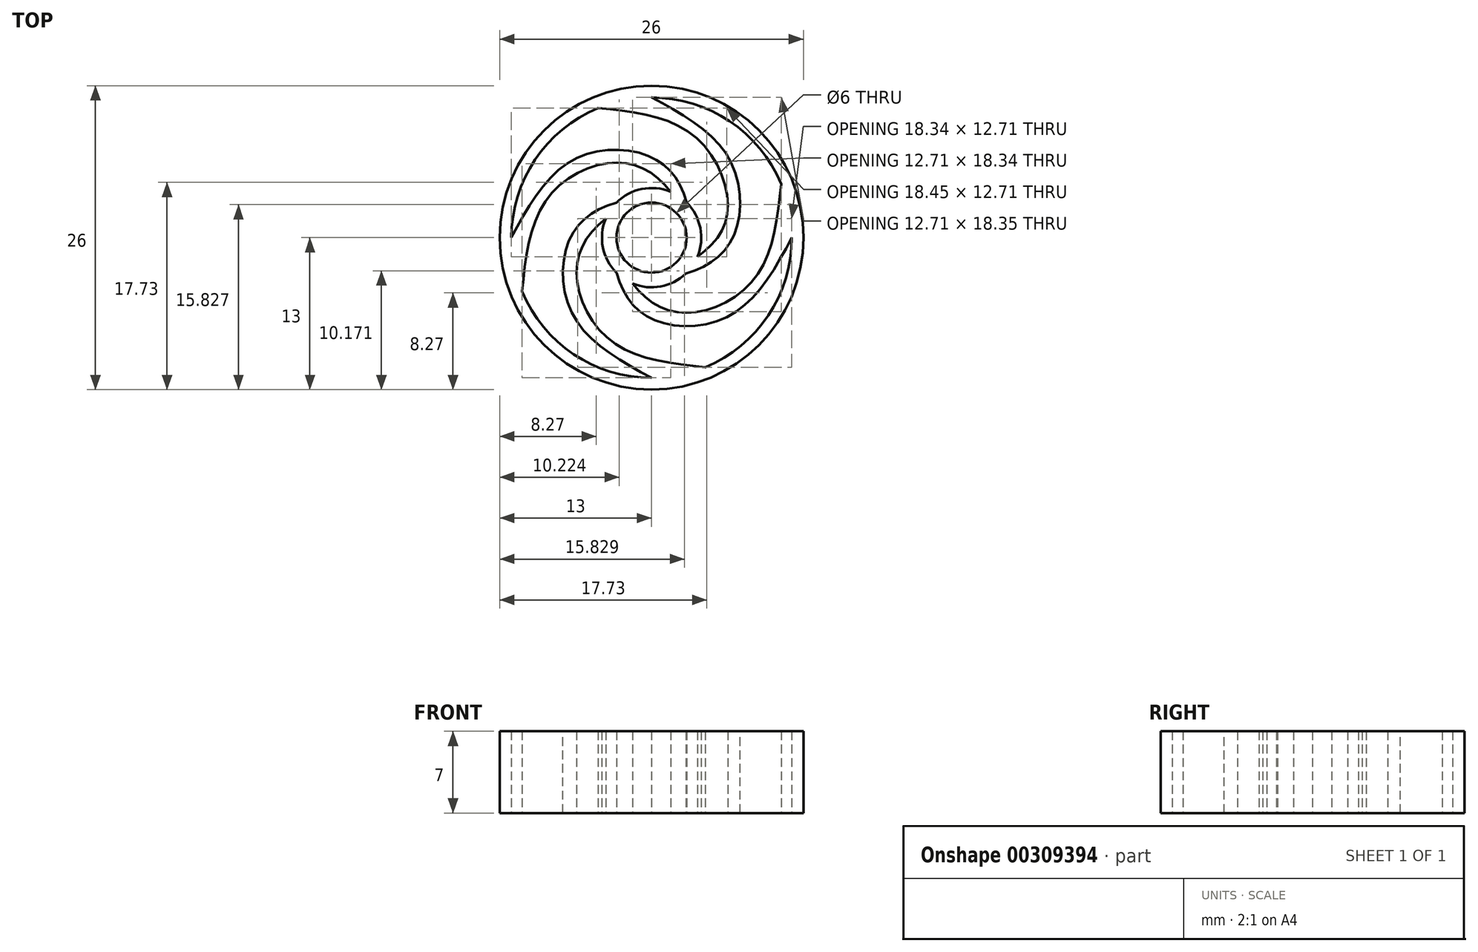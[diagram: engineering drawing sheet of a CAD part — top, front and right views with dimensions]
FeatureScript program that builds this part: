
annotation { "Feature Type Name" : "Feature", "Feature Type Description" : "" }
export const myFeature = defineFeature(function(context is Context, id is Id, definition is map)
    precondition{}
    {
        {
            var Q0;
            Q0=qCreatedBy(makeId("Top.planeOp"),FACE);
            var sketch = newSketch(context, id + "F0", { "sketchPlane" : qUnion([Q0])});
            skCircle(sketch, "E0", {"center": v(0, 0) * mm, "radius": 3 * mm});
            skCircle(sketch, "E1", {"center": v(0, 0) * mm, "radius": 4.25 * mm});
            skCircle(sketch, "E2", {"center": v(0, 0) * mm, "radius": 12 * mm});
            skFitSpline(sketch, "E3", {"points": [v(-11.09, 4.6) * mm, v(-3.61, 8.73) * mm, v(2.66, 6.42) * mm, v(3.93, 1.63) * mm], "startDerivative": vector(18.7, 15.37) * mm, "endDerivative": vector(-2.28, -19.06) * mm});
            skFitSpline(sketch, "E4", {"points": [v(-8.49, 8.49) * mm, v(0, 9.44) * mm, v(4.85, 4.98) * mm, v(4.25, 0) * mm], "startDerivative": vector(23.2, 7) * mm, "endDerivative": vector(-9.1, -16.95) * mm});
            skFitSpline(sketch, "E5", {"points": [v(-4.6, 11.09) * mm, v(3.61, 8.73) * mm, v(6.52, 2.4) * mm, v(3.93, -1.63) * mm], "startDerivative": vector(24.04, -2.2) * mm, "endDerivative": vector(-15.71, -10.92) * mm});
            skFitSpline(sketch, "E6", {"points": [v(0, 12) * mm, v(6.68, 6.68) * mm, v(6.95, 0) * mm, v(2.93, -3.08) * mm], "startDerivative": vector(21.35, -11.4) * mm, "endDerivative": vector(-18.29, -5.43) * mm});
            skFitSpline(sketch, "E7", {"points": [v(4.6, 11.09) * mm, v(8.73, 3.61) * mm, v(6.42, -2.66) * mm, v(1.63, -3.93) * mm], "startDerivative": vector(15.37, -18.7) * mm, "endDerivative": vector(-19.06, 2.28) * mm});
            skFitSpline(sketch, "E8", {"points": [v(8.49, 8.49) * mm, v(9.44, 0) * mm, v(4.92, -4.92) * mm, v(0, -4.25) * mm], "startDerivative": vector(7.04, -23.16) * mm, "endDerivative": vector(-16.74, 9.4) * mm});
            skFitSpline(sketch, "E9", {"points": [v(11.09, 4.6) * mm, v(8.73, -3.61) * mm, v(2.66, -6.42) * mm, v(-1.63, -3.93) * mm], "startDerivative": vector(-2.32, -24.08) * mm, "endDerivative": vector(-11.66, 15.2) * mm});
            skFitSpline(sketch, "E10", {"points": [v(12, 0) * mm, v(6.68, -6.68) * mm, v(0, -6.95) * mm, v(-3, -3) * mm], "startDerivative": vector(-11.4, -21.36) * mm, "endDerivative": vector(-5.2, 18.45) * mm});
            skFitSpline(sketch, "E11", {"points": [v(11.09, -4.6) * mm, v(3.61, -8.73) * mm, v(-2.66, -6.42) * mm, v(-3.93, -1.63) * mm], "startDerivative": vector(-18.7, -15.37) * mm, "endDerivative": vector(2.26, 19.04) * mm});
            skFitSpline(sketch, "E12", {"points": [v(8.49, -8.49) * mm, v(-0.02, -9.44) * mm, v(-4.92, -4.92) * mm, v(-4.25, 0) * mm], "startDerivative": vector(-23.2, -7.05) * mm, "endDerivative": vector(9.37, 16.72) * mm});
            skFitSpline(sketch, "E13", {"points": [v(4.6, -11.09) * mm, v(-3.61, -8.73) * mm, v(-6.42, -2.66) * mm, v(-3.93, 1.63) * mm], "startDerivative": vector(-24.1, 2.36) * mm, "endDerivative": vector(15.06, 11.86) * mm});
            skFitSpline(sketch, "E14", {"points": [v(0, -12) * mm, v(-6.72, -6.64) * mm, v(-6.95, 0) * mm, v(-3, 3) * mm], "startDerivative": vector(-21.46, 11.5) * mm, "endDerivative": vector(18.43, 5.21) * mm});
            skFitSpline(sketch, "E15", {"points": [v(-4.6, -11.09) * mm, v(-8.73, -3.61) * mm, v(-6.42, 2.66) * mm, v(-1.63, 3.93) * mm], "startDerivative": vector(-15.37, 18.7) * mm, "endDerivative": vector(19.04, -2.26) * mm});
            skFitSpline(sketch, "E16", {"points": [v(-8.49, -8.49) * mm, v(-9.44, 0) * mm, v(-4.92, 4.92) * mm, v(0, 4.25) * mm], "startDerivative": vector(-7.04, 23.16) * mm, "endDerivative": vector(16.72, -9.38) * mm});
            skFitSpline(sketch, "E17", {"points": [v(-11.09, -4.6) * mm, v(-8.73, 3.61) * mm, v(-2.66, 6.42) * mm, v(1.63, 3.93) * mm], "startDerivative": vector(2.36, 24.1) * mm, "endDerivative": vector(11.86, -15.06) * mm});
            skFitSpline(sketch, "E18", {"points": [v(-12, 0) * mm, v(-6.68, 6.68) * mm, v(0, 6.88) * mm, v(3, 3) * mm], "startDerivative": vector(11.4, 21.36) * mm, "endDerivative": vector(5.2, -18.45) * mm});
            skCircle(sketch, "E19", {"center": v(0, 0) * mm, "radius": 13 * mm});
            skSolve(sketch);
        }
        {
            var Q0;
            Q0=makeQuery(id+"F0.imprint","IMPRINT",FACE,{"disambiguationData":[TD([[makeQuery(id+"F0.imprint","IMPRINT",EDGE,{"derivedFrom":sQuery(id+"F0.wireOp",EDGE,"E19")}),1.0]])]});
            var Q1;
            {var subQ0=sQuery(id+"F0.wireOp",EDGE,"E9");Q1=makeQuery(id+"F0.imprint","IMPRINT",FACE,{"disambiguationData":[TD([[makeQuery(id+"F0.imprint","IMPRINT",EDGE,{"derivedFrom":subQ0}),1.0]])]});}
            var Q2;
            {var subQ0=sQuery(id+"F0.wireOp",EDGE,"E5");Q2=makeQuery(id+"F0.imprint","IMPRINT",FACE,{"disambiguationData":[TD([[makeQuery(id+"F0.imprint","IMPRINT",EDGE,{"derivedFrom":subQ0}),1.0]])]});}
            var Q3;
            {var subQ0=sQuery(id+"F0.wireOp",EDGE,"E17");Q3=makeQuery(id+"F0.imprint","IMPRINT",FACE,{"disambiguationData":[TD([[makeQuery(id+"F0.imprint","IMPRINT",EDGE,{"derivedFrom":subQ0}),1.0]])]});}
            var Q4;
            {var subQ0=sQuery(id+"F0.wireOp",EDGE,"E13");Q4=makeQuery(id+"F0.imprint","IMPRINT",FACE,{"disambiguationData":[TD([[makeQuery(id+"F0.imprint","IMPRINT",EDGE,{"derivedFrom":subQ0}),1.0]])]});}
            var Q5;
            Q5=makeQuery(id+"F0.imprint","IMPRINT",FACE,{"disambiguationData":[TD([[makeQuery(id+"F0.imprint","IMPRINT",EDGE,{"derivedFrom":sQuery(id+"F0.wireOp",EDGE,"E0")}),-1.0]])]});
            extrude(context, id + "F1", {"entities" : qUnion([Q0, Q1, Q2, Q3, Q4, Q5]), "depth" : 7 * mm});
        }
    });
